# Revit family: Genelec_4030
name_source: partatom
category: Generic Models
units: mm (PartAtom-declared; Revit-internal decimal feet)

## family parameters
Always vertical = No
Can host rebar = No
Cut with Voids When Loaded = No
Maintain Annotation Orientation = No
Part Type = Normal
Room Calculation Point = Yes
Round Connector Dimension = Use Diameter
Shared = No
Work Plane-Based = No

## types (2) — shared parameters
Accuracy of Frequency Response = ± 2 dB (54 Hz - 20 kHz)
Acoustic Axis = 175
BIMobject category = Audio Electronics
Color = RAL_9018_Papyrus White
Connections = 1 x Euroblock Analog Input
1 x Euroblock Analog Input
1 x Euroblock Analog Input
1 x Euroblock Analog Input
Default Elevation = 1200 mm
Depth = 178 mm
Description = The 4030C Active Installation Loudspeaker offers crystal clear sound and round-the-clock reliability, making it the natural choice for wide range of installations.
Dispersion Angle = H 120° V 100°
Driver Dimensions = ⌀ 130 mm Woofer + ⌀ 19 mm Tweeter
Export Type to IFC As = IfcAudioVisualApplianceType
Finish Type = Die cast aluminium
Frequency Response = 47 Hz - 25 kHz (-6 dB)
Height = 285 mm
IFC Classification = Electric Appliance
IFC Name = 4030C
Line Drawing = https://assets.ctfassets.net
Mains Voltage = 100-240 VAC 50/60Hz
Manufacturer = GENELEC
Manufacturer Country = Finland
Max. short term sine wave acoustic output  on axis in half space, averaged from 100Hz to 3 kHz = ≥104 dB
Maximum long term RMS acoustic output in same conditions with IEC weighted noise (limited by driver unit protection circuit) = ≥96 dB
Model = 4030C
Model Description = Active Installation Speaker
Model Image = https://images.ctfassets.net
Model Name = 4030C
Mounting Type = Includes mount: 4000-410B/W
Power Consumption = 60 W
Power consumption Idle = ≤3 W
Power consumption Standby = ≤0.5 W (ISS Active)
Price List Description = Recycled-aluminium cabinet with tightly controlled directivity and minimum diffraction for excellent performance. Both drivers have metal protection grilles, with 130 mm (5 in) LF and 19 mm (3/4 in) HF transducers. Integrated crossover and Class D amplifiers 50 W + 50 W.  Max. SPL 104 dB, frequency response 47 Hz - 25 kHz  (- 6 dB). 

Room response controls on rear panel to compensate the placement and room effects. On-Off switch on the rear panel.  Dimensions: H 285 x W 189 x D 178 mm, weight 4,9 kg.
Product Family = Installation Speaker
Product Group = 4000 Series Installation Speakers
Self-generated Noise = ≤5 dB
Type IFC Predefined Type = SPEAKER
Type Image = <None>
URL = https://www.genelec.com
Uniclass 2.0 Description = Sound Amplifiers
Weight = 4.9
Width = 189 mm

## per-type parameters (varying)
| type | Horizontal | Vertical |
| 4030 Horizontal | Yes | No |
| 4030 Vertical | No | Yes |

## geometry (parser evidence)
native form markers: Sweep x3
no freeform markers — native parametric forms only
